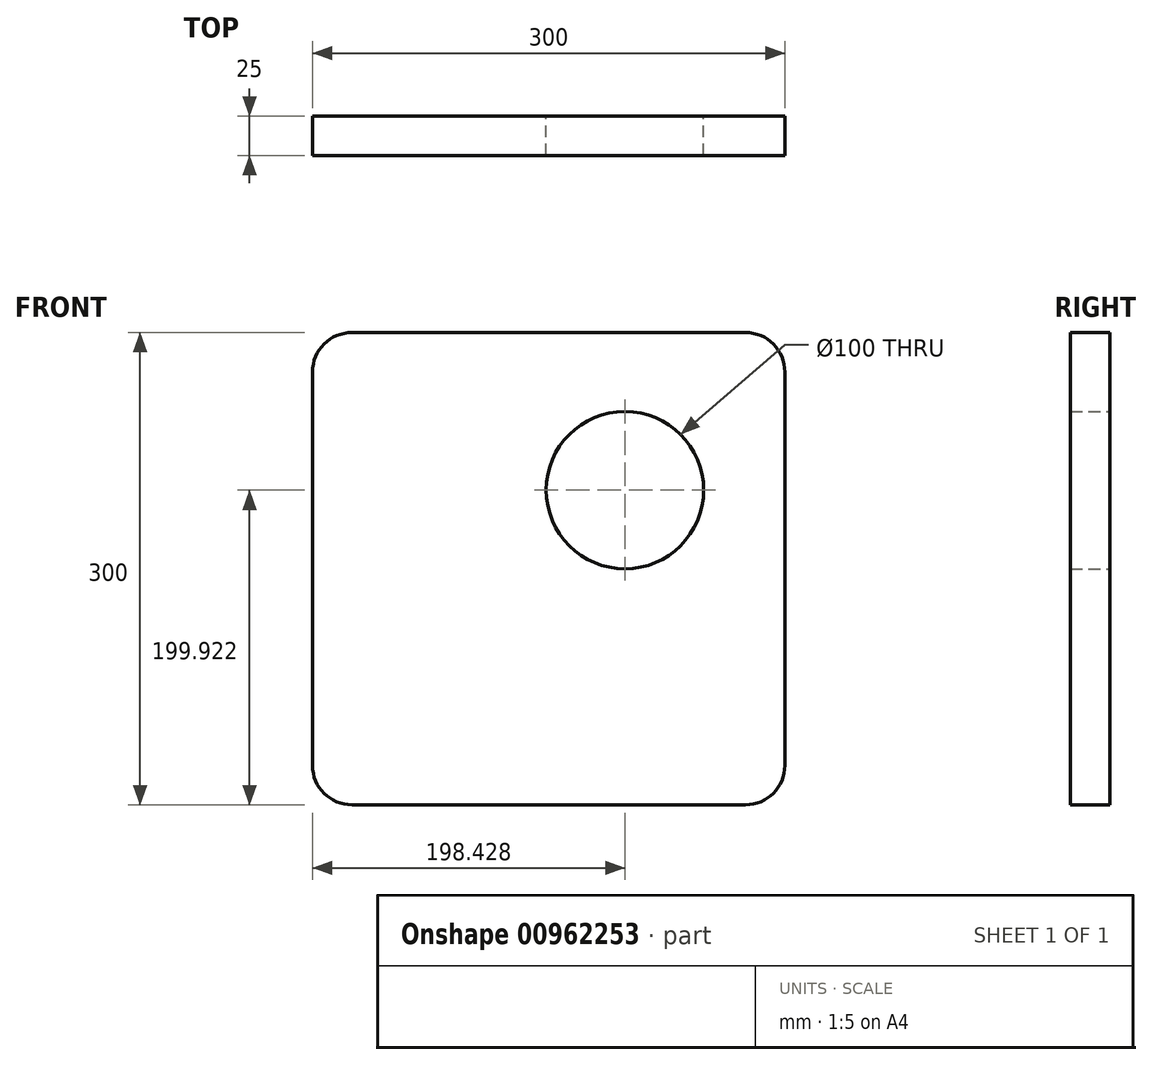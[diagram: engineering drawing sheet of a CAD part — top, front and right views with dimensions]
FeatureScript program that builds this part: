
annotation { "Feature Type Name" : "Feature", "Feature Type Description" : "" }
export const myFeature = defineFeature(function(context is Context, id is Id, definition is map)
    precondition{}
    {
        {
            var Q0;
            Q0=qCreatedBy(makeId("Front.planeOp"),FACE);
            var sketch = newSketch(context, id + "F0", { "sketchPlane" : qUnion([Q0])});
            skLineSegment(sketch, "E0.bottom", {"start": v(25, 0) * mm, "end": v(275, 0) * mm});
            skLineSegment(sketch, "E0.top", {"start": v(25, 300) * mm, "end": v(275, 300) * mm});
            skLineSegment(sketch, "E0.left", {"start": v(0, 25) * mm, "end": v(0, 275) * mm});
            skLineSegment(sketch, "E0.right", {"start": v(300, 25) * mm, "end": v(300, 275) * mm});
            skCircle(sketch, "E1", {"center": v(198.43, 199.92) * mm, "radius": 50 * mm});
            skPoint(sketch, "E2.visualSharp", {"position": v(300, 300) * mm});
            skArc(sketch, "E2.filletArc", {"start": v(300, 275) * mm, "mid": v(292.68, 292.68) * mm, "end": v(275, 300) * mm});
            skPoint(sketch, "E3.visualSharp", {"position": v(0, 300) * mm});
            skArc(sketch, "E3.filletArc", {"start": v(25, 300) * mm, "mid": v(7.32, 292.68) * mm, "end": v(0, 275) * mm});
            skPoint(sketch, "E4.visualSharp", {"position": v(0, 0) * mm});
            skArc(sketch, "E4.filletArc", {"start": v(0, 25) * mm, "mid": v(7.32, 7.32) * mm, "end": v(25, 0) * mm});
            skPoint(sketch, "E5.visualSharp", {"position": v(300, 0) * mm});
            skArc(sketch, "E5.filletArc", {"start": v(275, 0) * mm, "mid": v(292.68, 7.32) * mm, "end": v(300, 25) * mm});
            skSolve(sketch);
        }
        {
            var Q0;
            Q0=makeQuery(id+"F0.imprint","IMPRINT",FACE,{"disambiguationData":[TD([[makeQuery(id+"F0.imprint","IMPRINT",EDGE,{"derivedFrom":sQuery(id+"F0.wireOp",EDGE,"E0.bottom")}),1.0]])]});
            var Q1;
            {var subQ1=sQuery(id+"F0.wireOp",EDGE,"E0.top");Q1=makeQuery(id+"F0.imprint","IMPRINT",FACE,{"disambiguationData":[TD([[makeQuery(id+"F0.imprint","IMPRINT",EDGE,{"derivedFrom":subQ1}),-1.0]])]});}
            extrude(context, id + "F1", {"entities" : qUnion([Q0, Q1]), "depth" : 25 * mm, "offsetDistance" : 25 * mm});
        }
    });
